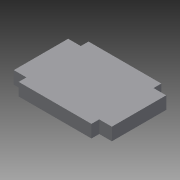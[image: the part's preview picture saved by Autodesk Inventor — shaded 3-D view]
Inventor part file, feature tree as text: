
AUTODESK INVENTOR PART (.ipt)
format: ipt  version: 2013 (Build 170138000, 138)  size: 98,304 bytes
history: native  units: mm
features: other x2, extrude x1, sketch x1
ambient origin geometry x8: Origin, YZ Plane, XZ Plane, XY Plane, X Axis, Y Axis, Z Axis, Center Point
feature tree (4):
  other  "Blocks"
  extrude  "Extrusion4"  Depth=3.0mm
  sketch  "Sketch1"  dims[d0=3.0mm d2=3.0mm d3=0.1mm d7=22.5mm d8=12.4mm d9=4.5mm d10=4.5mm d11=2.0mm d12=2.0mm d36=18.75mm d37=18.0mm d38=3.25mm d39=14.0mm d40=3.25mm d41=0.0mm]
  other  "Block1"
